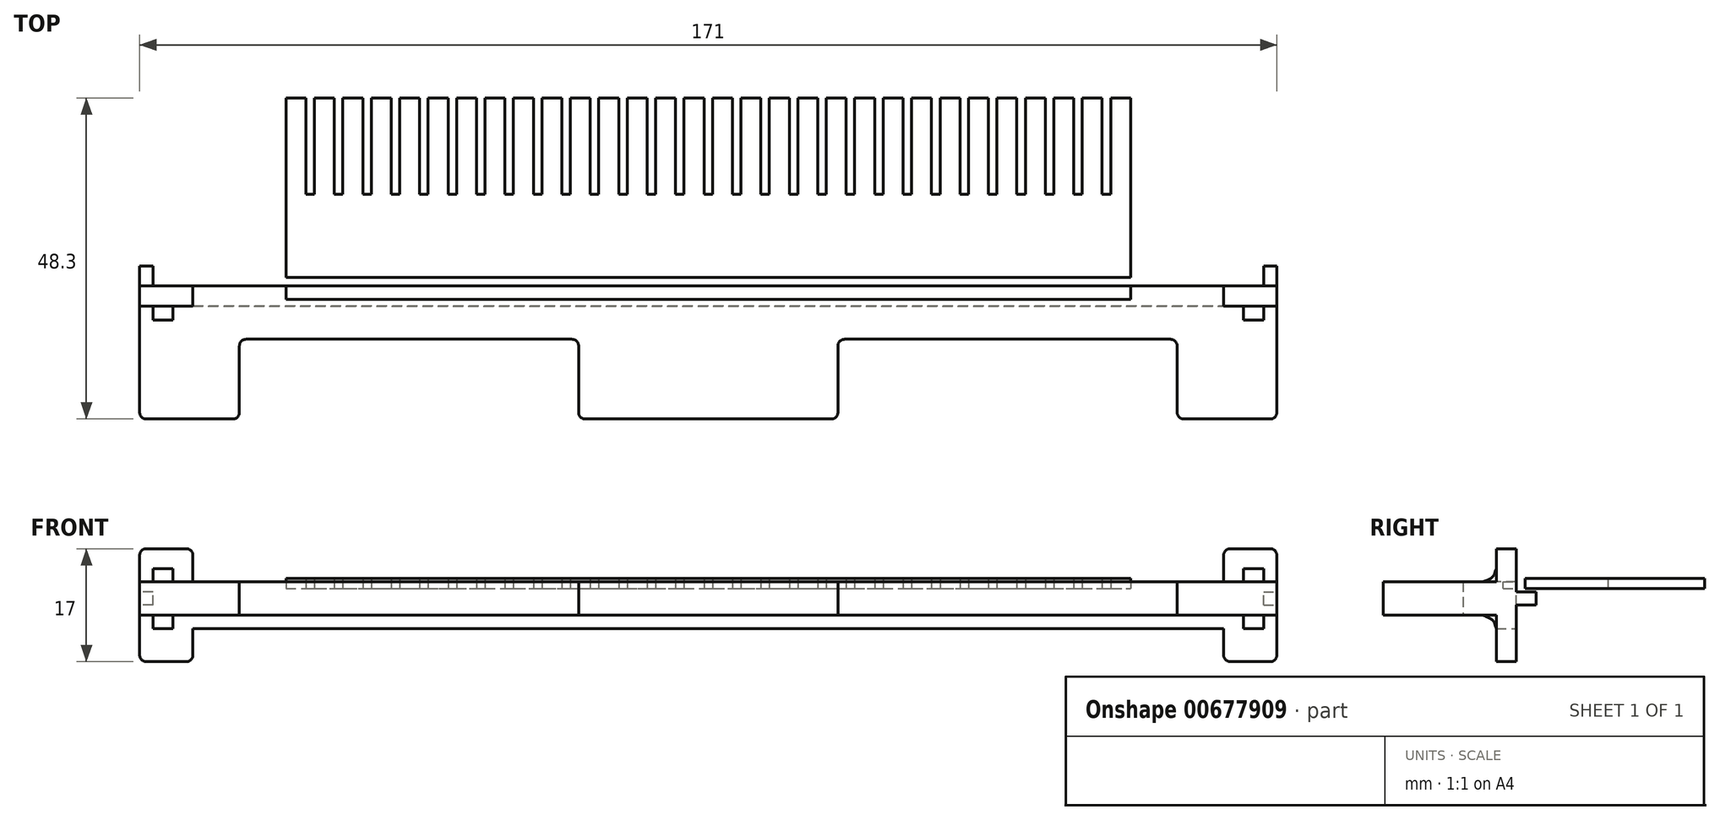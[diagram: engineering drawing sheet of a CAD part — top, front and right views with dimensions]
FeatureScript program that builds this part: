
annotation { "Feature Type Name" : "Feature", "Feature Type Description" : "" }
export const myFeature = defineFeature(function(context is Context, id is Id, definition is map)
    precondition{}
    {
        {
            var Q0;
            Q0=qCreatedBy(makeId("Top.planeOp"),FACE);
            var sketch = newSketch(context, id + "F0", { "sketchPlane" : qUnion([Q0])});
            skLineSegment(sketch, "E0.bottom", {"start": v(-85.5, 20) * mm, "end": v(85.5, 20) * mm});
            skLineSegment(sketch, "E0.top", {"start": v(-85.5, 0) * mm, "end": v(-70.5, 0) * mm});
            skLineSegment(sketch, "E0.left", {"start": v(-85.5, 20) * mm, "end": v(-85.5, 0) * mm});
            skLineSegment(sketch, "E0.right", {"start": v(85.5, 20) * mm, "end": v(85.5, 0) * mm});
            skLineSegment(sketch, "E1", {"start": v(-70.5, 12) * mm, "end": v(-70.5, 0) * mm});
            skLineSegment(sketch, "E2", {"start": v(-70.5, 12) * mm, "end": v(-19.5, 12) * mm});
            skPoint(sketch, "E3", {"position": v(0, 0) * mm});
            skLineSegment(sketch, "E4.MirrorCS", {"start": v(70.5, 12) * mm, "end": v(70.5, 0) * mm});
            skLineSegment(sketch, "E5", {"start": v(-19.5, 12) * mm, "end": v(-19.5, 0) * mm});
            skLineSegment(sketch, "E6.MirrorCS", {"start": v(19.5, 12) * mm, "end": v(19.5, 0) * mm});
            skLineSegment(sketch, "E7.trimOffspring", {"start": v(-19.5, 0) * mm, "end": v(19.5, 0) * mm});
            skLineSegment(sketch, "E8.trimOffspring", {"start": v(19.5, 12) * mm, "end": v(70.5, 12) * mm});
            skLineSegment(sketch, "E9.trimOffspring", {"start": v(70.5, 0) * mm, "end": v(85.5, 0) * mm});
            skPoint(sketch, "E10.orphan", {"position": v(19.5, 20) * mm});
            skPoint(sketch, "E11.orphan", {"position": v(70.5, 20) * mm});
            skPoint(sketch, "E12.orphan", {"position": v(-19.5, 20) * mm});
            skPoint(sketch, "E13.orphan", {"position": v(-70.5, 20) * mm});
            skSolve(sketch);
        }
        {
            var Q0;
            Q0=makeQuery(id+"F0.imprint","IMPRINT",FACE,{"disambiguationData":[TD([[makeQuery(id+"F0.imprint","IMPRINT",EDGE,{"derivedFrom":sQuery(id+"F0.wireOp",EDGE,"E0.bottom")}),-1.0]])]});
            extrude(context, id + "F1", {"entities" : qUnion([Q0]), "depth" : 5 * mm, "offsetDistance" : 25 * mm});
        }
        {
            var Q0;
            Q0=makeQuery(id+"F1.opExtrude","SWEPT_FACE",FACE,{"disambiguationData":[OSD([sQuery(id+"F0.wireOp",EDGE,"E0.bottom")])]});
            var sketch = newSketch(context, id + "F2", { "sketchPlane" : qUnion([Q0])});
            skLineSegment(sketch, "E14.bottom", {"start": v(-77.5, -7) * mm, "end": v(-85.5, -7) * mm});
            skLineSegment(sketch, "E14.top", {"start": v(-77.5, 10) * mm, "end": v(-85.5, 10) * mm});
            skLineSegment(sketch, "E14.left", {"start": v(-77.5, -7) * mm, "end": v(-77.5, 10) * mm});
            skPoint(sketch, "E14.middle", {"position": v(-85.5, 2.5) * mm});
            skLineSegment(sketch, "E15", {"start": v(-85.5, 10) * mm, "end": v(-85.5, -7) * mm});
            skLineSegment(sketch, "E16.MirrorCS", {"start": v(85.5, 10) * mm, "end": v(85.5, -7) * mm});
            skPoint(sketch, "E17.MirrorP", {"position": v(85.5, 2.5) * mm});
            skLineSegment(sketch, "E18.MirrorCS", {"start": v(77.5, -7) * mm, "end": v(85.5, -7) * mm});
            skLineSegment(sketch, "E19.MirrorCS", {"start": v(77.5, 10) * mm, "end": v(85.5, 10) * mm});
            skLineSegment(sketch, "E20.MirrorCS", {"start": v(77.5, -7) * mm, "end": v(77.5, 10) * mm});
            skLineSegment(sketch, "E21.bottom", {"start": v(-83.5, 1.5) * mm, "end": v(-85.5, 1.5) * mm});
            skLineSegment(sketch, "E21.top", {"start": v(-83.5, 3.5) * mm, "end": v(-85.5, 3.5) * mm});
            skLineSegment(sketch, "E21.left", {"start": v(-83.5, 1.5) * mm, "end": v(-83.5, 3.5) * mm});
            skLineSegment(sketch, "E21.right", {"start": v(-85.5, 1.5) * mm, "end": v(-85.5, 3.5) * mm});
            skPoint(sketch, "E21.middle", {"position": v(-84.5, 2.5) * mm});
            skLineSegment(sketch, "E22.MirrorCS", {"start": v(83.5, 1.5) * mm, "end": v(85.5, 1.5) * mm});
            skLineSegment(sketch, "E23.MirrorCS", {"start": v(83.5, 3.5) * mm, "end": v(85.5, 3.5) * mm});
            skLineSegment(sketch, "E24.MirrorCS", {"start": v(83.5, 1.5) * mm, "end": v(83.5, 3.5) * mm});
            skLineSegment(sketch, "E25.MirrorCS", {"start": v(85.5, 1.5) * mm, "end": v(85.5, 3.5) * mm});
            skPoint(sketch, "E26.MirrorP", {"position": v(84.5, 2.5) * mm});
            skSolve(sketch);
        }
        {
            var Q0;
            {var subQ3=sQuery(id+"F2.wireOp",EDGE,"E19.MirrorCS");Q0=makeQuery(id+"F2.imprint","IMPRINT",FACE,{"disambiguationData":[TD([[makeQuery(id+"F2.imprint","IMPRINT",EDGE,{"derivedFrom":subQ3}),-1.0]])]});}
            var Q1;
            {var subQ3=sQuery(id+"F2.wireOp",EDGE,"E18.MirrorCS");Q1=makeQuery(id+"F2.imprint","IMPRINT",FACE,{"disambiguationData":[TD([[makeQuery(id+"F2.imprint","IMPRINT",EDGE,{"derivedFrom":subQ3}),1.0]])]});}
            var Q2;
            {var subQ6=sQuery(id+"F2.wireOp",EDGE,"E22.MirrorCS");Q2=makeQuery(id+"F2.imprint","IMPRINT",FACE,{"disambiguationData":[TD([[makeQuery(id+"F2.imprint","IMPRINT",EDGE,{"derivedFrom":subQ6}),-1.0]])]});}
            var Q3;
            Q3=makeQuery(id+"F2.imprint","IMPRINT",FACE,{"disambiguationData":[TD([[makeQuery(id+"F2.imprint","IMPRINT",EDGE,{"derivedFrom":sQuery(id+"F2.wireOp",EDGE,"E22.MirrorCS")}),1.0]])]});
            var Q4;
            Q4=makeQuery(id+"F2.imprint","IMPRINT",FACE,{"disambiguationData":[TD([[makeQuery(id+"F2.imprint","IMPRINT",EDGE,{"derivedFrom":sQuery(id+"F2.wireOp",EDGE,"E21.bottom")}),-1.0]])]});
            var Q5;
            {var subQ0=sQuery(id+"F2.wireOp",EDGE,"E14.top");Q5=makeQuery(id+"F2.imprint","IMPRINT",FACE,{"disambiguationData":[TD([[makeQuery(id+"F2.imprint","IMPRINT",EDGE,{"derivedFrom":subQ0}),1.0]])]});}
            var Q6;
            {var subQ6=sQuery(id+"F2.wireOp",EDGE,"E21.bottom");Q6=makeQuery(id+"F2.imprint","IMPRINT",FACE,{"disambiguationData":[TD([[makeQuery(id+"F2.imprint","IMPRINT",EDGE,{"derivedFrom":subQ6}),1.0]])]});}
            var Q7;
            {var subQ0=sQuery(id+"F2.wireOp",EDGE,"E14.bottom");Q7=makeQuery(id+"F2.imprint","IMPRINT",FACE,{"disambiguationData":[TD([[makeQuery(id+"F2.imprint","IMPRINT",EDGE,{"derivedFrom":subQ0}),-1.0]])]});}
            extrude(context, id + "F3", {"entities" : qUnion([Q0, Q1, Q2, Q3, Q4, Q5, Q6, Q7]), "operationType" : NewBodyOperationType.ADD, "oppositeDirection" : true, "depth" : 3 * mm, "offsetDistance" : 25 * mm});
        }
        {
            var Q0;
            Q0=makeQuery(id+"F2.imprint","IMPRINT",FACE,{"disambiguationData":[TD([[makeQuery(id+"F2.imprint","IMPRINT",EDGE,{"derivedFrom":sQuery(id+"F2.wireOp",EDGE,"E22.MirrorCS")}),1.0]])]});
            var Q1;
            Q1=makeQuery(id+"F2.imprint","IMPRINT",FACE,{"disambiguationData":[TD([[makeQuery(id+"F2.imprint","IMPRINT",EDGE,{"derivedFrom":sQuery(id+"F2.wireOp",EDGE,"E21.bottom")}),-1.0]])]});
            extrude(context, id + "F4", {"entities" : qUnion([Q0, Q1]), "operationType" : NewBodyOperationType.ADD, "depth" : 3 * mm, "offsetDistance" : 25 * mm});
        }
        {
            var Q0;
            {var subQ0=sQuery(id+"F2.wireOp",EDGE,"E14.left");var subQ1=sQuery(id+"F0.wireOp",EDGE,"E0.bottom");var subQ2=makeQuery(id+"F1.opExtrude","CAP_EDGE",EDGE,{"disambiguationData":[OSD([subQ1])],"isStart":true});var subQ3=makeQuery(id+"F2.imprint","INTERSECT",VERTEX,{"derivedFrom":[subQ2,subQ0]});Q0=makeQuery(id+"F2.imprint","IMPRINT",FACE,{"disambiguationData":[TD([[makeQuery(id+"F2.imprint","IMPRINT",EDGE,{"disambiguationData":[TD([[subQ3,-1.0]])],"derivedFrom":subQ0}),-1.0]])]});}
            var sketch = newSketch(context, id + "F5", { "sketchPlane" : qUnion([Q0])});
            skLineSegment(sketch, "E27.bottom", {"start": v(0, 70.7) * mm, "end": v(-171, 70.7) * mm});
            skLineSegment(sketch, "E27.top", {"start": v(0, 77.7) * mm, "end": v(-171, 77.7) * mm});
            skLineSegment(sketch, "E27.left", {"start": v(0, 70.7) * mm, "end": v(0, 77.7) * mm});
            skLineSegment(sketch, "E27.right", {"start": v(-171, 70.7) * mm, "end": v(-171, 77.7) * mm});
            skPoint(sketch, "E27.middle", {"position": v(-85.5, 74.2) * mm});
            skPoint(sketch, "E28", {"position": v(-85.5, 77.7) * mm});
            skPoint(sketch, "E29", {"position": v(0, 5) * mm});
            skLineSegment(sketch, "E30.0", {"start": v(77.5, 5) * mm, "end": v(-77.5, 5) * mm, "construction": true});
            skLineSegment(sketch, "E31.bottom", {"start": v(-24.5, 76.7) * mm, "end": v(-146.5, 76.7) * mm});
            skLineSegment(sketch, "E31.top", {"start": v(-24.5, 77.7) * mm, "end": v(-146.5, 77.7) * mm});
            skLineSegment(sketch, "E31.left", {"start": v(-24.5, 76.7) * mm, "end": v(-24.5, 77.7) * mm});
            skLineSegment(sketch, "E31.right", {"start": v(-146.5, 76.7) * mm, "end": v(-146.5, 77.7) * mm});
            skPoint(sketch, "E31.middle", {"position": v(-85.5, 77.2) * mm});
            skLineSegment(sketch, "E32.bottom", {"start": v(85.5, -2) * mm, "end": v(-85.5, -2) * mm});
            skLineSegment(sketch, "E32.top", {"start": v(85.5, 5) * mm, "end": v(-85.5, 5) * mm});
            skLineSegment(sketch, "E32.left", {"start": v(85.5, -2) * mm, "end": v(85.5, 5) * mm});
            skLineSegment(sketch, "E32.right", {"start": v(-85.5, -2) * mm, "end": v(-85.5, 5) * mm});
            skPoint(sketch, "E32.middle", {"position": v(0, 1.5) * mm});
            skLineSegment(sketch, "E33.bottom", {"start": v(63.5, 4) * mm, "end": v(-63.5, 4) * mm});
            skLineSegment(sketch, "E33.top", {"start": v(63.5, 5) * mm, "end": v(-63.5, 5) * mm});
            skLineSegment(sketch, "E33.left", {"start": v(63.5, 4) * mm, "end": v(63.5, 5) * mm});
            skLineSegment(sketch, "E33.right", {"start": v(-63.5, 4) * mm, "end": v(-63.5, 5) * mm});
            skPoint(sketch, "E33.middle", {"position": v(0, 4.5) * mm});
            skSolve(sketch);
        }
        {
            var Q0;
            Q0=makeQuery(id+"F5.imprint","IMPRINT",FACE,{"disambiguationData":[TD([[makeQuery(id+"F5.imprint","IMPRINT",EDGE,{"derivedFrom":sQuery(id+"F5.wireOp",EDGE,"E32.bottom")}),-1.0]])]});
            var Q1;
            Q1=makeQuery(id+"F5.imprint","IMPRINT",FACE,{"disambiguationData":[TD([[makeQuery(id+"F5.imprint","IMPRINT",EDGE,{"derivedFrom":sQuery(id+"F5.wireOp",EDGE,"E33.bottom")}),1.0]])]});
            extrude(context, id + "F6", {"entities" : qUnion([Q0, Q1]), "operationType" : NewBodyOperationType.ADD, "oppositeDirection" : true, "depth" : 3 * mm, "offsetDistance" : 25 * mm});
        }
        {
            var Q0;
            Q0=makeQuery(id+"F1.opExtrude","SWEPT_EDGE",EDGE,{"disambiguationData":[OSD([sQuery(id+"F0.wireOp",EDGE,"E0.top"),sQuery(id+"F0.wireOp",EDGE,"E1")])]});
            var Q1;
            Q1=makeQuery(id+"F1.opExtrude","SWEPT_EDGE",EDGE,{"disambiguationData":[OSD([sQuery(id+"F0.wireOp",EDGE,"E5"),sQuery(id+"F0.wireOp",EDGE,"E7.trimOffspring")])]});
            var Q2;
            Q2=makeQuery(id+"F1.opExtrude","SWEPT_EDGE",EDGE,{"disambiguationData":[OSD([sQuery(id+"F0.wireOp",EDGE,"E6.MirrorCS"),sQuery(id+"F0.wireOp",EDGE,"E7.trimOffspring")])]});
            var Q3;
            Q3=makeQuery(id+"F1.opExtrude","SWEPT_EDGE",EDGE,{"disambiguationData":[OSD([sQuery(id+"F0.wireOp",EDGE,"E4.MirrorCS"),sQuery(id+"F0.wireOp",EDGE,"E9.trimOffspring")])]});
            var Q4;
            Q4=makeQuery(id+"F1.opExtrude","SWEPT_EDGE",EDGE,{"disambiguationData":[OSD([sQuery(id+"F0.wireOp",EDGE,"E0.right"),sQuery(id+"F0.wireOp",EDGE,"E9.trimOffspring")])]});
            var Q5;
            Q5=makeQuery(id+"F1.opExtrude","SWEPT_EDGE",EDGE,{"disambiguationData":[OSD([sQuery(id+"F0.wireOp",EDGE,"E4.MirrorCS"),sQuery(id+"F0.wireOp",EDGE,"E8.trimOffspring")])]});
            var Q6;
            Q6=makeQuery(id+"F1.opExtrude","SWEPT_EDGE",EDGE,{"disambiguationData":[OSD([sQuery(id+"F0.wireOp",EDGE,"E6.MirrorCS"),sQuery(id+"F0.wireOp",EDGE,"E8.trimOffspring")])]});
            var Q7;
            Q7=makeQuery(id+"F1.opExtrude","SWEPT_EDGE",EDGE,{"disambiguationData":[OSD([sQuery(id+"F0.wireOp",EDGE,"E2"),sQuery(id+"F0.wireOp",EDGE,"E5")])]});
            var Q8;
            Q8=makeQuery(id+"F1.opExtrude","SWEPT_EDGE",EDGE,{"disambiguationData":[OSD([sQuery(id+"F0.wireOp",EDGE,"E1"),sQuery(id+"F0.wireOp",EDGE,"E2")])]});
            var Q9;
            Q9=makeQuery(id+"F1.opExtrude","SWEPT_EDGE",EDGE,{"disambiguationData":[OSD([sQuery(id+"F0.wireOp",EDGE,"E0.top"),sQuery(id+"F0.wireOp",EDGE,"E0.left")])]});
            var Q10;
            Q10=makeQuery(id+"F3.opExtrude","SWEPT_EDGE",EDGE,{"disambiguationData":[OSD([sQuery(id+"F2.wireOp",EDGE,"E19.MirrorCS"),sQuery(id+"F2.wireOp",EDGE,"E20.MirrorCS")])]});
            var Q11;
            Q11=makeQuery(id+"F3.opExtrude","SWEPT_EDGE",EDGE,{"disambiguationData":[OSD([sQuery(id+"F2.wireOp",EDGE,"E16.MirrorCS"),sQuery(id+"F2.wireOp",EDGE,"E19.MirrorCS")])]});
            var Q12;
            Q12=makeQuery(id+"F3.opExtrude","SWEPT_EDGE",EDGE,{"disambiguationData":[OSD([sQuery(id+"F2.wireOp",EDGE,"E14.top"),sQuery(id+"F2.wireOp",EDGE,"E15")])]});
            var Q13;
            Q13=makeQuery(id+"F3.opExtrude","SWEPT_EDGE",EDGE,{"disambiguationData":[OSD([sQuery(id+"F2.wireOp",EDGE,"E14.top"),sQuery(id+"F2.wireOp",EDGE,"E14.left")])]});
            var Q14;
            Q14=makeQuery(id+"F3.opExtrude","SWEPT_EDGE",EDGE,{"disambiguationData":[OSD([sQuery(id+"F2.wireOp",EDGE,"E14.bottom"),sQuery(id+"F2.wireOp",EDGE,"E15")])]});
            var Q15;
            Q15=makeQuery(id+"F3.opExtrude","SWEPT_EDGE",EDGE,{"disambiguationData":[OSD([sQuery(id+"F2.wireOp",EDGE,"E14.bottom"),sQuery(id+"F2.wireOp",EDGE,"E14.left")])]});
            var Q16;
            Q16=makeQuery(id+"F3.opExtrude","SWEPT_EDGE",EDGE,{"disambiguationData":[OSD([sQuery(id+"F2.wireOp",EDGE,"E16.MirrorCS"),sQuery(id+"F2.wireOp",EDGE,"E18.MirrorCS")])]});
            var Q17;
            Q17=makeQuery(id+"F3.opExtrude","SWEPT_EDGE",EDGE,{"disambiguationData":[OSD([sQuery(id+"F2.wireOp",EDGE,"E18.MirrorCS"),sQuery(id+"F2.wireOp",EDGE,"E20.MirrorCS")])]});
            fillet(context, id + "F7", {"entities" : qUnion([Q0, Q1, Q2, Q3, Q4, Q5, Q6, Q7, Q8, Q9, Q10, Q11, Q12, Q13, Q14, Q15, Q16, Q17]), "radius" : 1 * mm, "tangentPropagation" : true, "allowEdgeOverflow" : false});
        }
        {
            var Q0;
            Q0=makeQuery(id+"F5.imprint","IMPRINT",FACE,{"disambiguationData":[TD([[makeQuery(id+"F5.imprint","IMPRINT",EDGE,{"derivedFrom":sQuery(id+"F5.wireOp",EDGE,"E33.bottom")}),1.0]])]});
            extrude(context, id + "F8", {"entities" : qUnion([Q0]), "operationType" : NewBodyOperationType.ADD, "oppositeDirection" : true, "depth" : 3 * mm, "offsetDistance" : 25 * mm});
        }
        {
            var Q0;
            Q0=makeQuery(id+"F5.imprint","IMPRINT",FACE,{"disambiguationData":[TD([[makeQuery(id+"F5.imprint","IMPRINT",EDGE,{"derivedFrom":sQuery(id+"F5.wireOp",EDGE,"E33.bottom")}),-1.0]])]});
            extrude(context, id + "F9", {"entities" : qUnion([Q0]), "operationType" : NewBodyOperationType.REMOVE, "oppositeDirection" : true, "depth" : 2 * mm, "offsetDistance" : 25 * mm});
        }
        {
            var Q0;
            Q0=makeQuery(id+"F9.boolean.opBoolean","COPY",FACE,{"derivedFrom":makeQuery(id+"F9.opExtrude","SWEPT_FACE",FACE,{"disambiguationData":[OSD([sQuery(id+"F5.wireOp",EDGE,"E33.bottom")])]})});
            var sketch = newSketch(context, id + "F10", { "sketchPlane" : qUnion([Q0])});
            skLineSegment(sketch, "E34.bottom", {"start": v(-63.5, 21.3) * mm, "end": v(63.5, 21.3) * mm});
            skLineSegment(sketch, "E34.left", {"start": v(-63.5, 21.3) * mm, "end": v(-63.5, 48.3) * mm});
            skLineSegment(sketch, "E34.right", {"start": v(63.5, 21.3) * mm, "end": v(63.5, 48.3) * mm});
            skLineSegment(sketch, "E35.right", {"start": v(-60.5, 48.3) * mm, "end": v(-60.5, 33.8) * mm});
            skLineSegment(sketch, "E36", {"start": v(-60.5, 33.8) * mm, "end": v(-59.22, 33.8) * mm});
            skLineSegment(sketch, "E37.1.0.0", {"start": v(-56.22, 48.3) * mm, "end": v(-56.22, 33.8) * mm});
            skLineSegment(sketch, "E37.1.0.1", {"start": v(-56.22, 33.8) * mm, "end": v(-54.95, 33.8) * mm});
            skLineSegment(sketch, "E37.2.0.0", {"start": v(-51.95, 48.3) * mm, "end": v(-51.95, 33.8) * mm});
            skLineSegment(sketch, "E37.2.0.1", {"start": v(-51.95, 33.8) * mm, "end": v(-50.67, 33.8) * mm});
            skLineSegment(sketch, "E37.3.0.0", {"start": v(-47.67, 48.3) * mm, "end": v(-47.67, 33.8) * mm});
            skLineSegment(sketch, "E37.3.0.1", {"start": v(-47.67, 33.8) * mm, "end": v(-46.4, 33.8) * mm});
            skLineSegment(sketch, "E37.4.0.0", {"start": v(-43.4, 48.3) * mm, "end": v(-43.4, 33.8) * mm});
            skLineSegment(sketch, "E37.4.0.1", {"start": v(-43.4, 33.8) * mm, "end": v(-42.12, 33.8) * mm});
            skLineSegment(sketch, "E37.5.0.0", {"start": v(-39.12, 48.3) * mm, "end": v(-39.12, 33.8) * mm});
            skLineSegment(sketch, "E37.5.0.1", {"start": v(-39.12, 33.8) * mm, "end": v(-37.84, 33.8) * mm});
            skLineSegment(sketch, "E37.6.0.0", {"start": v(-34.84, 48.3) * mm, "end": v(-34.84, 33.8) * mm});
            skLineSegment(sketch, "E37.6.0.1", {"start": v(-34.84, 33.8) * mm, "end": v(-33.57, 33.8) * mm});
            skLineSegment(sketch, "E37.7.0.0", {"start": v(-30.57, 48.3) * mm, "end": v(-30.57, 33.8) * mm});
            skLineSegment(sketch, "E37.7.0.1", {"start": v(-30.57, 33.8) * mm, "end": v(-29.3, 33.8) * mm});
            skLineSegment(sketch, "E37.8.0.0", {"start": v(-26.3, 48.3) * mm, "end": v(-26.3, 33.8) * mm});
            skLineSegment(sketch, "E37.8.0.1", {"start": v(-26.3, 33.8) * mm, "end": v(-25.02, 33.8) * mm});
            skLineSegment(sketch, "E37.9.0.0", {"start": v(-22.02, 48.3) * mm, "end": v(-22.02, 33.8) * mm});
            skLineSegment(sketch, "E37.9.0.1", {"start": v(-22.02, 33.8) * mm, "end": v(-20.74, 33.8) * mm});
            skLineSegment(sketch, "E37.10.0.0", {"start": v(-17.74, 48.3) * mm, "end": v(-17.74, 33.8) * mm});
            skLineSegment(sketch, "E37.10.0.1", {"start": v(-17.74, 33.8) * mm, "end": v(-16.46, 33.8) * mm});
            skLineSegment(sketch, "E37.11.0.0", {"start": v(-13.46, 48.3) * mm, "end": v(-13.46, 33.8) * mm});
            skLineSegment(sketch, "E37.11.0.1", {"start": v(-13.46, 33.8) * mm, "end": v(-12.19, 33.8) * mm});
            skLineSegment(sketch, "E37.12.0.0", {"start": v(-9.19, 48.3) * mm, "end": v(-9.19, 33.8) * mm});
            skLineSegment(sketch, "E37.12.0.1", {"start": v(-9.19, 33.8) * mm, "end": v(-7.91, 33.8) * mm});
            skLineSegment(sketch, "E37.13.0.0", {"start": v(-4.91, 48.3) * mm, "end": v(-4.91, 33.8) * mm});
            skLineSegment(sketch, "E37.13.0.1", {"start": v(-4.91, 33.8) * mm, "end": v(-3.64, 33.8) * mm});
            skLineSegment(sketch, "E37.14.0.0", {"start": v(-0.64, 48.3) * mm, "end": v(-0.64, 33.8) * mm});
            skLineSegment(sketch, "E37.14.0.1", {"start": v(-0.64, 33.8) * mm, "end": v(0.64, 33.8) * mm});
            skLineSegment(sketch, "E37.15.0.0", {"start": v(3.64, 48.3) * mm, "end": v(3.64, 33.8) * mm});
            skLineSegment(sketch, "E37.15.0.1", {"start": v(3.64, 33.8) * mm, "end": v(4.92, 33.8) * mm});
            skLineSegment(sketch, "E37.16.0.0", {"start": v(7.92, 48.3) * mm, "end": v(7.92, 33.8) * mm});
            skLineSegment(sketch, "E37.16.0.1", {"start": v(7.92, 33.8) * mm, "end": v(9.2, 33.8) * mm});
            skLineSegment(sketch, "E37.17.0.0", {"start": v(12.2, 48.3) * mm, "end": v(12.2, 33.8) * mm});
            skLineSegment(sketch, "E37.17.0.1", {"start": v(12.2, 33.8) * mm, "end": v(13.47, 33.8) * mm});
            skLineSegment(sketch, "E37.18.0.0", {"start": v(16.47, 48.3) * mm, "end": v(16.47, 33.8) * mm});
            skLineSegment(sketch, "E37.18.0.1", {"start": v(16.47, 33.8) * mm, "end": v(17.74, 33.8) * mm});
            skLineSegment(sketch, "E37.19.0.0", {"start": v(20.74, 48.3) * mm, "end": v(20.74, 33.8) * mm});
            skLineSegment(sketch, "E37.19.0.1", {"start": v(20.74, 33.8) * mm, "end": v(22.02, 33.8) * mm});
            skLineSegment(sketch, "E37.20.0.0", {"start": v(25.02, 48.3) * mm, "end": v(25.02, 33.8) * mm});
            skLineSegment(sketch, "E37.20.0.1", {"start": v(25.02, 33.8) * mm, "end": v(26.3, 33.8) * mm});
            skLineSegment(sketch, "E37.21.0.0", {"start": v(29.3, 48.3) * mm, "end": v(29.3, 33.8) * mm});
            skLineSegment(sketch, "E37.21.0.1", {"start": v(29.3, 33.8) * mm, "end": v(30.57, 33.8) * mm});
            skLineSegment(sketch, "E37.22.0.0", {"start": v(33.57, 48.3) * mm, "end": v(33.57, 33.8) * mm});
            skLineSegment(sketch, "E37.22.0.1", {"start": v(33.57, 33.8) * mm, "end": v(34.85, 33.8) * mm});
            skLineSegment(sketch, "E37.23.0.0", {"start": v(37.85, 48.3) * mm, "end": v(37.85, 33.8) * mm});
            skLineSegment(sketch, "E37.23.0.1", {"start": v(37.85, 33.8) * mm, "end": v(39.12, 33.8) * mm});
            skLineSegment(sketch, "E37.24.0.0", {"start": v(42.12, 48.3) * mm, "end": v(42.12, 33.8) * mm});
            skLineSegment(sketch, "E37.24.0.1", {"start": v(42.12, 33.8) * mm, "end": v(43.4, 33.8) * mm});
            skLineSegment(sketch, "E37.25.0.0", {"start": v(46.4, 48.3) * mm, "end": v(46.4, 33.8) * mm});
            skLineSegment(sketch, "E37.25.0.1", {"start": v(46.4, 33.8) * mm, "end": v(47.68, 33.8) * mm});
            skLineSegment(sketch, "E37.26.0.0", {"start": v(50.68, 48.3) * mm, "end": v(50.68, 33.8) * mm});
            skLineSegment(sketch, "E37.26.0.1", {"start": v(50.68, 33.8) * mm, "end": v(51.95, 33.8) * mm});
            skLineSegment(sketch, "E37.27.0.0", {"start": v(54.95, 48.3) * mm, "end": v(54.95, 33.8) * mm});
            skLineSegment(sketch, "E37.27.0.1", {"start": v(54.95, 33.8) * mm, "end": v(56.23, 33.8) * mm});
            skLineSegment(sketch, "E37.28.0.0", {"start": v(59.23, 48.3) * mm, "end": v(59.23, 33.8) * mm});
            skLineSegment(sketch, "E37.28.0.1", {"start": v(59.23, 33.8) * mm, "end": v(60.5, 33.8) * mm});
            skLineSegment(sketch, "E37.direction1", {"start": v(-60.5, 33.8) * mm, "end": v(-56.22, 33.8) * mm, "construction": true});
            skLineSegment(sketch, "E38", {"start": v(-59.22, 48.3) * mm, "end": v(-59.22, 33.8) * mm});
            skLineSegment(sketch, "E39", {"start": v(-54.95, 33.8) * mm, "end": v(-54.95, 48.3) * mm});
            skLineSegment(sketch, "E40", {"start": v(-50.67, 48.3) * mm, "end": v(-50.67, 33.8) * mm});
            skLineSegment(sketch, "E41", {"start": v(-46.4, 33.8) * mm, "end": v(-46.4, 48.3) * mm});
            skLineSegment(sketch, "E42", {"start": v(-42.12, 48.3) * mm, "end": v(-42.12, 33.8) * mm});
            skLineSegment(sketch, "E43", {"start": v(-37.84, 48.3) * mm, "end": v(-37.84, 33.8) * mm});
            skLineSegment(sketch, "E44", {"start": v(-33.57, 48.3) * mm, "end": v(-33.57, 33.8) * mm});
            skLineSegment(sketch, "E45", {"start": v(-29.3, 48.3) * mm, "end": v(-29.3, 33.8) * mm});
            skLineSegment(sketch, "E46", {"start": v(-25.02, 33.8) * mm, "end": v(-25.02, 48.3) * mm});
            skLineSegment(sketch, "E47", {"start": v(-20.74, 33.8) * mm, "end": v(-20.74, 48.3) * mm});
            skLineSegment(sketch, "E48", {"start": v(-16.46, 33.8) * mm, "end": v(-16.46, 48.3) * mm});
            skLineSegment(sketch, "E49", {"start": v(-12.19, 48.3) * mm, "end": v(-12.19, 33.8) * mm});
            skLineSegment(sketch, "E50", {"start": v(-7.91, 33.8) * mm, "end": v(-7.91, 48.3) * mm});
            skLineSegment(sketch, "E51", {"start": v(-3.64, 48.3) * mm, "end": v(-3.64, 33.8) * mm});
            skLineSegment(sketch, "E52", {"start": v(0.64, 33.8) * mm, "end": v(0.64, 48.3) * mm});
            skLineSegment(sketch, "E53", {"start": v(4.92, 48.3) * mm, "end": v(4.92, 33.8) * mm});
            skLineSegment(sketch, "E54", {"start": v(9.2, 33.8) * mm, "end": v(9.2, 48.3) * mm});
            skLineSegment(sketch, "E55", {"start": v(13.47, 48.3) * mm, "end": v(13.47, 33.8) * mm});
            skLineSegment(sketch, "E56", {"start": v(17.74, 33.8) * mm, "end": v(17.74, 48.3) * mm});
            skLineSegment(sketch, "E57", {"start": v(22.02, 33.8) * mm, "end": v(22.02, 48.3) * mm});
            skLineSegment(sketch, "E58", {"start": v(26.3, 48.3) * mm, "end": v(26.3, 33.8) * mm});
            skLineSegment(sketch, "E59", {"start": v(30.57, 33.8) * mm, "end": v(30.57, 48.3) * mm});
            skLineSegment(sketch, "E60", {"start": v(34.85, 33.8) * mm, "end": v(34.85, 48.3) * mm});
            skLineSegment(sketch, "E61", {"start": v(39.12, 33.8) * mm, "end": v(39.12, 48.3) * mm});
            skLineSegment(sketch, "E62", {"start": v(43.4, 48.3) * mm, "end": v(43.4, 33.8) * mm});
            skLineSegment(sketch, "E63", {"start": v(47.68, 33.8) * mm, "end": v(47.68, 48.3) * mm});
            skLineSegment(sketch, "E64", {"start": v(51.95, 48.3) * mm, "end": v(51.95, 33.8) * mm});
            skLineSegment(sketch, "E65", {"start": v(60.5, 33.8) * mm, "end": v(60.5, 48.3) * mm});
            skLineSegment(sketch, "E66", {"start": v(56.23, 33.8) * mm, "end": v(56.23, 48.3) * mm});
            skPoint(sketch, "E67.visualSharp", {"position": v(-63.5, 21.3) * mm});
            skLineSegment(sketch, "E67.filletArc", {"start": v(-63.5, 21.3) * mm, "end": v(-63.5, 21.3) * mm});
            skLineSegment(sketch, "E68", {"start": v(-63.5, 48.3) * mm, "end": v(-60.5, 48.3) * mm});
            skLineSegment(sketch, "E69.trimOffspring", {"start": v(-59.22, 48.3) * mm, "end": v(-56.22, 48.3) * mm});
            skLineSegment(sketch, "E70.trimOffspring", {"start": v(-54.95, 48.3) * mm, "end": v(-51.95, 48.3) * mm});
            skLineSegment(sketch, "E71.trimOffspring", {"start": v(-50.67, 48.3) * mm, "end": v(-47.67, 48.3) * mm});
            skLineSegment(sketch, "E72.trimOffspring", {"start": v(-46.4, 48.3) * mm, "end": v(-43.4, 48.3) * mm});
            skLineSegment(sketch, "E73.trimOffspring", {"start": v(-42.12, 48.3) * mm, "end": v(-39.12, 48.3) * mm});
            skLineSegment(sketch, "E74.trimOffspring", {"start": v(-37.84, 48.3) * mm, "end": v(-34.84, 48.3) * mm});
            skLineSegment(sketch, "E75.trimOffspring", {"start": v(-33.57, 48.3) * mm, "end": v(-30.57, 48.3) * mm});
            skLineSegment(sketch, "E76.trimOffspring", {"start": v(-29.3, 48.3) * mm, "end": v(-26.3, 48.3) * mm});
            skLineSegment(sketch, "E77.trimOffspring", {"start": v(-25.02, 48.3) * mm, "end": v(-22.02, 48.3) * mm});
            skLineSegment(sketch, "E78.trimOffspring", {"start": v(-20.74, 48.3) * mm, "end": v(-17.74, 48.3) * mm});
            skLineSegment(sketch, "E79.trimOffspring", {"start": v(-16.46, 48.3) * mm, "end": v(-13.46, 48.3) * mm});
            skLineSegment(sketch, "E80.trimOffspring", {"start": v(-12.19, 48.3) * mm, "end": v(-9.19, 48.3) * mm});
            skLineSegment(sketch, "E81.trimOffspring", {"start": v(-7.91, 48.3) * mm, "end": v(-4.91, 48.3) * mm});
            skLineSegment(sketch, "E82.trimOffspring", {"start": v(-3.64, 48.3) * mm, "end": v(-0.64, 48.3) * mm});
            skLineSegment(sketch, "E83.trimOffspring", {"start": v(0.64, 48.3) * mm, "end": v(3.64, 48.3) * mm});
            skLineSegment(sketch, "E84.trimOffspring", {"start": v(4.92, 48.3) * mm, "end": v(7.92, 48.3) * mm});
            skLineSegment(sketch, "E85.trimOffspring", {"start": v(9.2, 48.3) * mm, "end": v(12.2, 48.3) * mm});
            skLineSegment(sketch, "E86.trimOffspring", {"start": v(13.47, 48.3) * mm, "end": v(16.47, 48.3) * mm});
            skLineSegment(sketch, "E87.trimOffspring", {"start": v(17.74, 48.3) * mm, "end": v(20.74, 48.3) * mm});
            skLineSegment(sketch, "E88.trimOffspring", {"start": v(22.02, 48.3) * mm, "end": v(25.02, 48.3) * mm});
            skLineSegment(sketch, "E89.trimOffspring", {"start": v(26.3, 48.3) * mm, "end": v(29.3, 48.3) * mm});
            skLineSegment(sketch, "E90.trimOffspring", {"start": v(30.57, 48.3) * mm, "end": v(33.57, 48.3) * mm});
            skLineSegment(sketch, "E91.trimOffspring", {"start": v(34.85, 48.3) * mm, "end": v(37.85, 48.3) * mm});
            skLineSegment(sketch, "E92.trimOffspring", {"start": v(39.12, 48.3) * mm, "end": v(42.12, 48.3) * mm});
            skLineSegment(sketch, "E93.trimOffspring", {"start": v(43.4, 48.3) * mm, "end": v(46.4, 48.3) * mm});
            skLineSegment(sketch, "E94.trimOffspring", {"start": v(47.68, 48.3) * mm, "end": v(50.68, 48.3) * mm});
            skLineSegment(sketch, "E95.trimOffspring", {"start": v(51.95, 48.3) * mm, "end": v(54.95, 48.3) * mm});
            skLineSegment(sketch, "E96.trimOffspring", {"start": v(56.23, 48.3) * mm, "end": v(59.23, 48.3) * mm});
            skLineSegment(sketch, "E97.trimOffspring", {"start": v(60.5, 48.3) * mm, "end": v(63.5, 48.3) * mm});
            skSolve(sketch);
        }
        {
            var Q0;
            Q0=makeQuery(id+"F10.imprint","IMPRINT",FACE,{"disambiguationData":[TD([[makeQuery(id+"F10.imprint","IMPRINT",EDGE,{"derivedFrom":sQuery(id+"F10.wireOp",EDGE,"E34.bottom")}),1.0]])]});
            extrude(context, id + "F11", {"entities" : qUnion([Q0]), "depth" : 1.5 * mm, "offsetDistance" : 25 * mm});
        }
        {
            var Q0;
            {var subQ0=sQuery(id+"F2.wireOp",EDGE,"E25.MirrorCS");Q0=makeQuery(id+"F4.boolean.opBoolean","MERGE",FACE,{"derivedFrom":[makeQuery(id+"F3.boolean.opBoolean","MERGE",FACE,{"derivedFrom":[makeQuery(id+"F1.opExtrude","SWEPT_FACE",FACE,{"disambiguationData":[OSD([sQuery(id+"F0.wireOp",EDGE,"E0.left")])]}),makeQuery(id+"F3.opExtrude","SWEPT_FACE",FACE,{"disambiguationData":[OSD([sQuery(id+"F2.wireOp",EDGE,"E16.MirrorCS"),subQ0])]})]}),makeQuery(id+"F4.opExtrude","SWEPT_FACE",FACE,{"disambiguationData":[OSD([subQ0])]})]});}
            var sketch = newSketch(context, id + "F12", { "sketchPlane" : qUnion([Q0])});
            skFitSpline(sketch, "E98", {"points": [v(-17, 7) * mm, v(-14.86, 5) * mm], "startDerivative": vector(1.4, -3.49) * mm, "endDerivative": vector(5.65, -1.83) * mm});
            skLineSegment(sketch, "E99", {"start": v(-17, 7) * mm, "end": v(-17, 5) * mm});
            skLineSegment(sketch, "E100", {"start": v(-17, 5) * mm, "end": v(-14.86, 5) * mm});
            skLineSegment(sketch, "E101", {"start": v(-1, 2.5) * mm, "end": v(-23, 2.5) * mm, "construction": true});
            skLineSegment(sketch, "E102.MirrorCS", {"start": v(-17, -2) * mm, "end": v(-17, 0) * mm});
            skFitSpline(sketch, "E103.MirrorCS", {"points": [v(-17, -2) * mm, v(-14.86, 0) * mm], "startDerivative": vector(1.4, 3.49) * mm, "endDerivative": vector(5.65, 1.83) * mm});
            skLineSegment(sketch, "E104.MirrorCS", {"start": v(-17, 0) * mm, "end": v(-14.86, 0) * mm});
            skSolve(sketch);
        }
        {
            var Q0;
            Q0=makeQuery(id+"F12.imprint","IMPRINT",FACE,{"disambiguationData":[TD([[makeQuery(id+"F12.imprint","IMPRINT",EDGE,{"derivedFrom":sQuery(id+"F12.wireOp",EDGE,"E98")}),-1.0]])]});
            var Q1;
            Q1=makeQuery(id+"F12.imprint","IMPRINT",FACE,{"disambiguationData":[TD([[makeQuery(id+"F12.imprint","IMPRINT",EDGE,{"derivedFrom":sQuery(id+"F12.wireOp",EDGE,"E102.MirrorCS")}),1.0]])]});
            extrude(context, id + "F13", {"entities" : qUnion([Q0, Q1]), "oppositeDirection" : true, "depth" : 5 * mm, "offsetDistance" : 25 * mm, "hasSecondDirection" : true, "secondDirectionOppositeDirection" : true, "secondDirectionDepth" : 2 * mm});
        }
        {
            var Q0;
            Q0=makeQuery(id+"F13.opExtrude","SWEPT_BODY",BODY,{"disambiguationData":[OSD([sQuery(id+"F12.wireOp",EDGE,"E98"),sQuery(id+"F12.wireOp",EDGE,"E99"),sQuery(id+"F12.wireOp",EDGE,"E100")])]});
            var Q1;
            Q1=makeQuery(id+"F13.opExtrude","SWEPT_BODY",BODY,{"disambiguationData":[OSD([sQuery(id+"F12.wireOp",EDGE,"E102.MirrorCS"),sQuery(id+"F12.wireOp",EDGE,"E103.MirrorCS"),sQuery(id+"F12.wireOp",EDGE,"E104.MirrorCS")])]});
            var Q2;
            Q2=qCreatedBy(makeId("Right.planeOp"),FACE);
            mirror(context, id + "F14", {"operationType" : NewBodyOperationType.ADD, "entities" : qUnion([Q0, Q1]), "mirrorPlane" : qUnion([Q2])});
        }
    });
